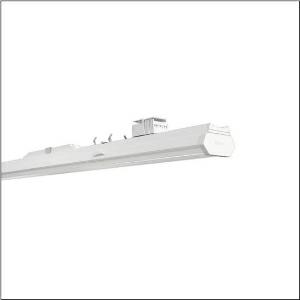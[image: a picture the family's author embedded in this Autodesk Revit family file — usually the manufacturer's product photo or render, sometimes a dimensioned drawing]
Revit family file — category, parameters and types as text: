
# Revit family: licross_r__11_protected_mo_51td11dn495g_7274
name_source: partatom
category: Lighting Fixtures
units: mm (PartAtom-declared; Revit-internal decimal feet)

## family parameters
Cut with Voids When Loaded = No
Host = Face
Light Source = No
Part Type = Normal
Room Calculation Point = No
Round Connector Dimension = Use Diameter
Shared = No

## types (1)
- --- (1 x LED, 9930 lm, 57.1 W, 4000K)
    Apparent Load = 57 VA
    CIE Flux Codes = 83 94 98 100 100
    Color Rendering = 80
    Color Temperature = 4000K
    Default Elevation = 1800 mm
    Description = Licross® 11 Protected MO, luminaire insert, of sheet steel, galvanised, coil coated, white, length: 1.500mm, width: 90mm, height: 101mm, LED rated luminous flux: 9.930lm, light colour: 840, control gear: DALI 2, with plug, 5-pole, with phase selection, mains connection: 220..240V, AC, 50/60Hz, rated input power: 57W, internal wiring halogen-free, primary light control with lens, of plastic, primary optical cover: cover, of PMMA, light emission: direct distribution, primary light characteristic: symmetric, protection rating (complete): IP54, insulation class (complete): insulation class I (protective earthing), certification: CE, ENEC, VDE, UKCA, protection symbol: D if used in an environment with non-conductive dust loads with corresponding accessories, impact resistance: IK06, permissible ambient temperature for indoor applications: -25..+35°C, corresponds to IFS (International Featured Standards) requirements for safety and quality in the food industry, reducing of maximum allowable ambient temperature of 5°C with ceiling mounting, LABS conformity tested according to VDMA 24364:2018-05, packaging unit: 1 piece
    Height = 92 mm
    Lamp = 1 x LED
    Lamp Light Flux = 9930 lm
    Lamp Power = 57.1 W
    Lamp count = 1
    Length = 1500 mm
    Luminous efficacy = 174 lm/W
    Manufacturer = Siteco
    ModVariant = No
    Model = 51TD11DN495G
    Mounting Place = Ceiling
    Mounting Type = Pendant
    Number of Poles = 1
    OnlyDefault = Yes
    Power Factor = 1
    Product Name = Licross® 11 Protected MO
    Product group = luminaire insert | ceiling pendant
    ProductGroupID = 902
    Protection Class = Protection class I
    Protection Degree = IP 54
    RLX_Detail_Level = 1
    RLX_Emergency_Light_Flux = 0 lm
    RLX_Emergency_Type = 0
    RLX_Emergency_Type_DB = No
    RlxData = <blob elided: 24157 chars, md5=024715c5>
    Socket = socket
    Standby Power = 0 W
    System Light Flux = 9930 lm
    System Power = 57 W
    Type Comments = factory setting: luminous flux: 100 % | dim-lin: 254 | 378 mA
    Type Image = l_1256145.jpg
    URL = http://relux.com
    VarID = @adj_122407
    Voltage = 0 V
    Weight = 0.00 kg
    Width = 88 mm

## geometry (parser evidence)
native form markers: Blend x4, Sweep x12
no freeform markers — native parametric forms only
